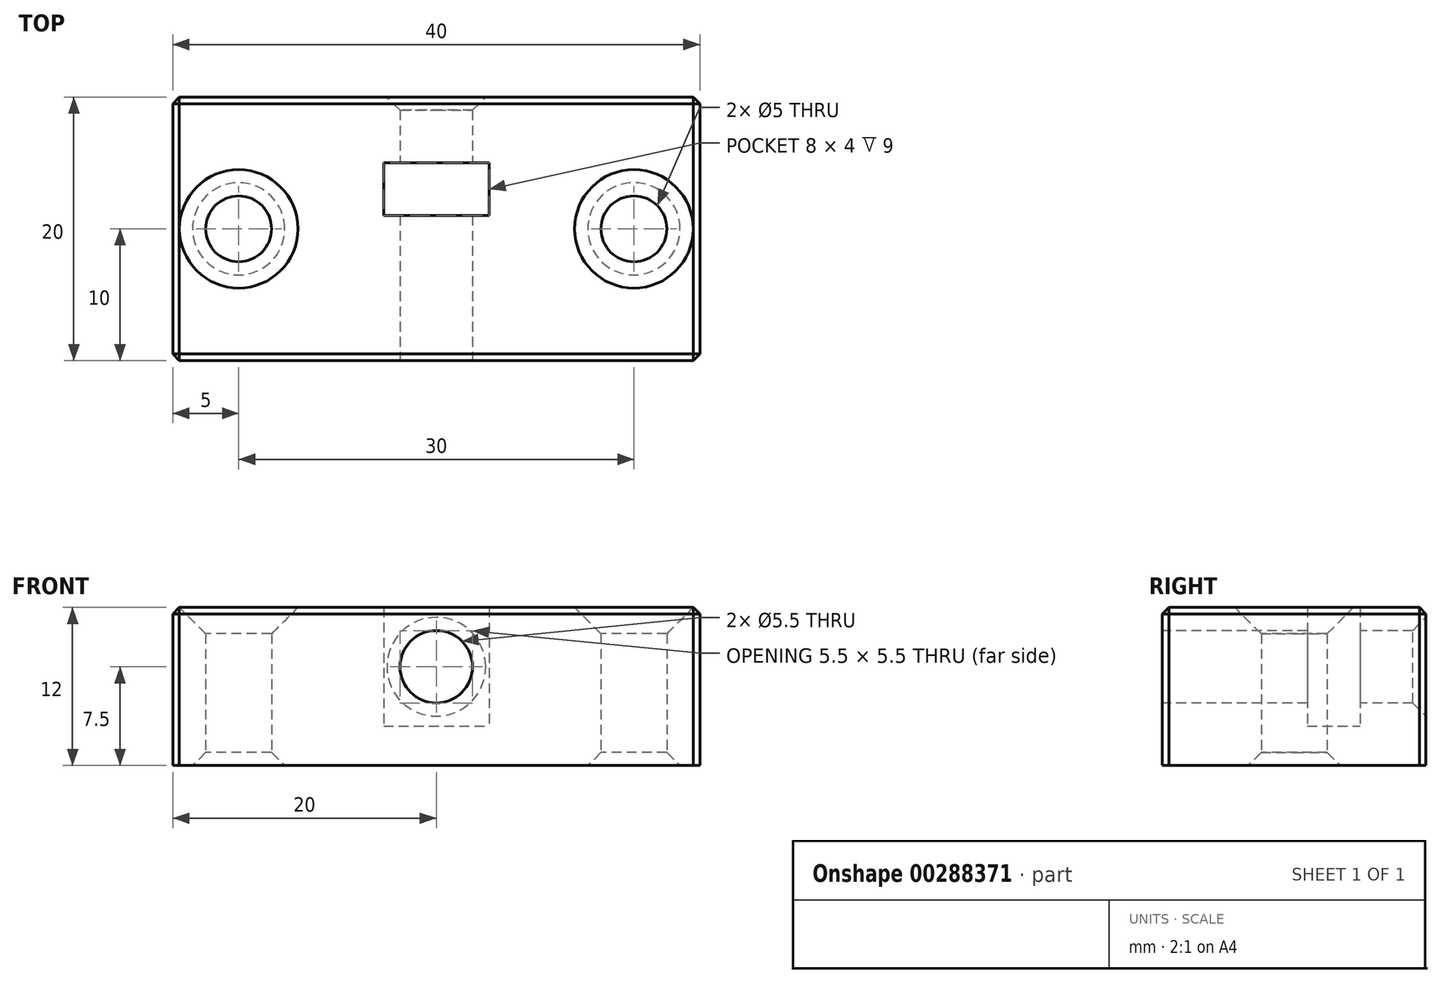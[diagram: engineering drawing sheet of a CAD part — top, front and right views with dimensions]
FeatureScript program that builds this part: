
annotation { "Feature Type Name" : "Feature", "Feature Type Description" : "" }
export const myFeature = defineFeature(function(context is Context, id is Id, definition is map)
    precondition{}
    {
        {
            var Q0;
            Q0=qCreatedBy(makeId("Top.planeOp"),FACE);
            var sketch = newSketch(context, id + "F0", { "sketchPlane" : qUnion([Q0])});
            skLineSegment(sketch, "E0.bottom", {"start": v(20, 10) * mm, "end": v(-20, 10) * mm});
            skLineSegment(sketch, "E0.top", {"start": v(20, -10) * mm, "end": v(-20, -10) * mm});
            skLineSegment(sketch, "E0.left", {"start": v(20, 10) * mm, "end": v(20, -10) * mm});
            skLineSegment(sketch, "E0.right", {"start": v(-20, 10) * mm, "end": v(-20, -10) * mm});
            skPoint(sketch, "E0.middle", {"position": v(0, 0) * mm});
            skLineSegment(sketch, "E1.bottom", {"start": v(-4, 1) * mm, "end": v(4, 1) * mm});
            skLineSegment(sketch, "E1.top", {"start": v(-4, 5) * mm, "end": v(4, 5) * mm});
            skLineSegment(sketch, "E1.left", {"start": v(-4, 1) * mm, "end": v(-4, 5) * mm});
            skLineSegment(sketch, "E1.right", {"start": v(4, 1) * mm, "end": v(4, 5) * mm});
            skLineSegment(sketch, "E2", {"start": v(-20, 0) * mm, "end": v(20, 0) * mm, "construction": true});
            skLineSegment(sketch, "E3", {"start": v(-15, 4.85) * mm, "end": v(-15, -5.64) * mm, "construction": true});
            skLineSegment(sketch, "E4", {"start": v(15, 3.6) * mm, "end": v(15, -6.88) * mm, "construction": true});
            skCircle(sketch, "E5", {"center": v(-15, 0) * mm, "radius": 2.5 * mm});
            skCircle(sketch, "E6", {"center": v(15, 0) * mm, "radius": 2.5 * mm});
            skSolve(sketch);
        }
        {
            var Q0;
            Q0 = qSketchRegion(id + "F0", true);
            extrude(context, id + "F1", {"entities" : qUnion([Q0]), "depth" : 12 * mm});
        }
        {
            var Q0;
            Q0=makeQuery(id+"F0.imprint","IMPRINT",FACE,{"disambiguationData":[TD([[makeQuery(id+"F0.imprint","IMPRINT",EDGE,{"derivedFrom":sQuery(id+"F0.wireOp",EDGE,"E1.bottom")}),1.0]])]});
            extrude(context, id + "F2", {"entities" : qUnion([Q0]), "operationType" : NewBodyOperationType.ADD, "depth" : 3 * mm});
        }
        {
            var Q0;
            Q0=makeQuery(id+"F1.opExtrude","SWEPT_FACE",FACE,{"disambiguationData":[OSD([sQuery(id+"F0.wireOp",EDGE,"E0.top")])]});
            var sketch = newSketch(context, id + "F3", { "sketchPlane" : qUnion([Q0])});
            skLineSegment(sketch, "E7", {"start": v(-20, 7.5) * mm, "end": v(20, 7.5) * mm, "construction": true});
            skLineSegment(sketch, "E8", {"start": v(0, 12) * mm, "end": v(0, 0) * mm, "construction": true});
            skCircle(sketch, "E9", {"center": v(0, 7.5) * mm, "radius": 2.75 * mm});
            skSolve(sketch);
        }
        {
            var Q0;
            Q0=makeQuery(id+"F3.imprint","IMPRINT",FACE,{"disambiguationData":[TD([[makeQuery(id+"F3.imprint","IMPRINT",EDGE,{"derivedFrom":sQuery(id+"F3.wireOp",EDGE,"E9")}),1.0]])]});
            extrude(context, id + "F4", {"entities" : qUnion([Q0]), "operationType" : NewBodyOperationType.REMOVE, "oppositeDirection" : true, "depth" : 25 * mm});
        }
        {
            var Q0;
            Q0=makeQuery(id+"F1.opExtrude","CAP_EDGE",EDGE,{"disambiguationData":[OSD([sQuery(id+"F0.wireOp",EDGE,"E5")])],"isStart":false});
            var Q1;
            Q1=makeQuery(id+"F1.opExtrude","CAP_EDGE",EDGE,{"disambiguationData":[OSD([sQuery(id+"F0.wireOp",EDGE,"E6")])],"isStart":false});
            chamfer(context, id + "F5", {"entities" : qUnion([Q0, Q1]), "width" : 2 * mm, "tangentPropagation" : true});
        }
        {
            var Q0;
            Q0=makeQuery(id+"F4.boolean.opBoolean","INTERSECT",EDGE,{"derivedFrom":[makeQuery(id+"F1.opExtrude","SWEPT_FACE",FACE,{"disambiguationData":[OSD([sQuery(id+"F0.wireOp",EDGE,"E0.bottom")])]}),makeQuery(id+"F4.opExtrude","SWEPT_FACE",FACE,{"disambiguationData":[OSD([sQuery(id+"F3.wireOp",EDGE,"E9")])]})]});
            var Q1;
            Q1=makeQuery(id+"F1.opExtrude","CAP_EDGE",EDGE,{"disambiguationData":[OSD([sQuery(id+"F0.wireOp",EDGE,"E5")])],"isStart":true});
            var Q2;
            Q2=makeQuery(id+"F1.opExtrude","CAP_EDGE",EDGE,{"disambiguationData":[OSD([sQuery(id+"F0.wireOp",EDGE,"E6")])],"isStart":true});
            var Q3;
            Q3=makeQuery(id+"F4.boolean.opBoolean","COPY",EDGE,{"derivedFrom":makeQuery(id+"F4.opExtrude","CAP_EDGE",EDGE,{"disambiguationData":[OSD([sQuery(id+"F3.wireOp",EDGE,"E9")])],"isStart":true})});
            chamfer(context, id + "F6", {"entities" : qUnion([Q0, Q1, Q2, Q3]), "width" : 1 * mm, "tangentPropagation" : true});
        }
        {
            var Q0;
            Q0=makeQuery(id+"F1.opExtrude","CAP_EDGE",EDGE,{"disambiguationData":[OSD([sQuery(id+"F0.wireOp",EDGE,"E0.bottom")])],"isStart":false});
            var Q1;
            Q1=makeQuery(id+"F1.opExtrude","CAP_EDGE",EDGE,{"disambiguationData":[OSD([sQuery(id+"F0.wireOp",EDGE,"E0.left")])],"isStart":false});
            var Q2;
            Q2=makeQuery(id+"F1.opExtrude","CAP_EDGE",EDGE,{"disambiguationData":[OSD([sQuery(id+"F0.wireOp",EDGE,"E0.top")])],"isStart":false});
            var Q3;
            Q3=makeQuery(id+"F1.opExtrude","CAP_EDGE",EDGE,{"disambiguationData":[OSD([sQuery(id+"F0.wireOp",EDGE,"E0.right")])],"isStart":false});
            var Q4;
            Q4=makeQuery(id+"F1.opExtrude","SWEPT_EDGE",EDGE,{"disambiguationData":[OSD([sQuery(id+"F0.wireOp",EDGE,"E0.bottom"),sQuery(id+"F0.wireOp",EDGE,"E0.right")])]});
            var Q5;
            Q5=makeQuery(id+"F1.opExtrude","SWEPT_EDGE",EDGE,{"disambiguationData":[OSD([sQuery(id+"F0.wireOp",EDGE,"E0.bottom"),sQuery(id+"F0.wireOp",EDGE,"E0.left")])]});
            var Q6;
            Q6=makeQuery(id+"F1.opExtrude","SWEPT_EDGE",EDGE,{"disambiguationData":[OSD([sQuery(id+"F0.wireOp",EDGE,"E0.top"),sQuery(id+"F0.wireOp",EDGE,"E0.left")])]});
            var Q7;
            Q7=makeQuery(id+"F1.opExtrude","SWEPT_EDGE",EDGE,{"disambiguationData":[OSD([sQuery(id+"F0.wireOp",EDGE,"E0.top"),sQuery(id+"F0.wireOp",EDGE,"E0.right")])]});
            chamfer(context, id + "F7", {"entities" : qUnion([Q0, Q1, Q2, Q3, Q4, Q5, Q6, Q7]), "width" : 0.5 * mm, "tangentPropagation" : true});
        }
    });
